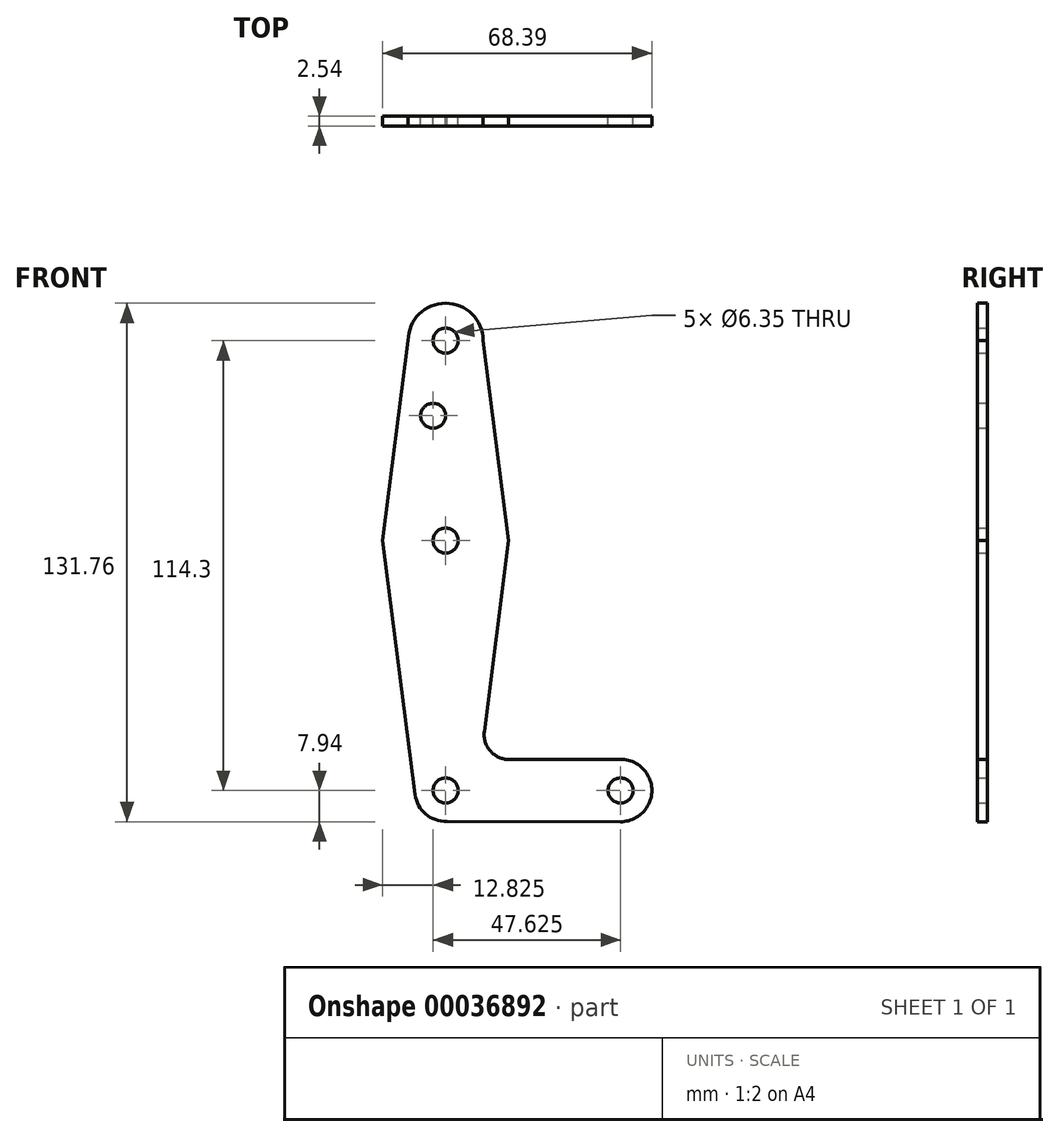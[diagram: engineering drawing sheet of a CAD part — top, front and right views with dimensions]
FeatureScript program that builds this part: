
annotation { "Feature Type Name" : "Feature", "Feature Type Description" : "" }
export const myFeature = defineFeature(function(context is Context, id is Id, definition is map)
    precondition{}
    {
        {
            var Q0;
            Q0=qCreatedBy(makeId("Front.planeOp"),FACE);
            var sketch = newSketch(context, id + "F0", { "sketchPlane" : qUnion([Q0])});
            skLineSegment(sketch, "E0", {"start": v(0, 50.8) * mm, "end": v(0, -63.5) * mm});
            skLineSegment(sketch, "E1", {"start": v(0, -63.5) * mm, "end": v(44.45, -63.5) * mm});
            skCircle(sketch, "E2", {"center": v(0, 50.8) * mm, "radius": 9.53 * mm});
            skCircle(sketch, "E3", {"center": v(0, 0) * mm, "radius": 15.88 * mm});
            skCircle(sketch, "E4", {"center": v(0, -63.5) * mm, "radius": 7.84 * mm});
            skCircle(sketch, "E5", {"center": v(44.45, -63.5) * mm, "radius": 7.94 * mm});
            skLineSegment(sketch, "E6", {"start": v(-9.52, 50.8) * mm, "end": v(-16, 0) * mm});
            skLineSegment(sketch, "E7", {"start": v(9.53, 50.8) * mm, "end": v(16, 0) * mm});
            skLineSegment(sketch, "E8", {"start": v(16, 0) * mm, "end": v(9.82, -48.47) * mm});
            skLineSegment(sketch, "E9", {"start": v(16.13, -55.62) * mm, "end": v(44.43, -55.56) * mm});
            skCircle(sketch, "E10", {"center": v(0, 50.8) * mm, "radius": 3.18 * mm});
            skCircle(sketch, "E11", {"center": v(44.45, -63.5) * mm, "radius": 3.18 * mm});
            skCircle(sketch, "E12", {"center": v(-3.17, 31.72) * mm, "radius": 3.18 * mm});
            skCircle(sketch, "E13", {"center": v(0, 0) * mm, "radius": 3.18 * mm});
            skLineSegment(sketch, "E14", {"start": v(-16, 0) * mm, "end": v(-7.78, -64.5) * mm});
            skCircle(sketch, "E15", {"center": v(0, -63.5) * mm, "radius": 3.18 * mm});
            skArc(sketch, "E16.filletArc", {"start": v(9.82, -48.47) * mm, "mid": v(11.36, -53.48) * mm, "end": v(16.13, -55.62) * mm});
            skLineSegment(sketch, "E17", {"start": v(0.28, -71.34) * mm, "end": v(44.43, -71.44) * mm});
            skSolve(sketch);
        }
        {
            var Q0;
            Q0 = qSketchRegion(id + "F0", true);
            extrude(context, id + "F1", {"entities" : qUnion([Q0]), "depth" : 2.54 * mm});
        }
        {
            var Q0;
            {var subQ0=sQuery(id+"F0.wireOp",EDGE,"E4");var subQ3=sQuery(id+"F0.wireOp",EDGE,"E0");var subQ4=makeQuery(id+"F0.imprint","INTERSECT",VERTEX,{"derivedFrom":[subQ3,subQ0]});Q0=makeQuery(id+"F0.imprint","IMPRINT",FACE,{"disambiguationData":[TD([[makeQuery(id+"F0.imprint","IMPRINT",EDGE,{"disambiguationData":[TD([[subQ4,-1.0]])],"derivedFrom":subQ3}),1.0]])]});}
            extrude(context, id + "F2", {"entities" : qUnion([Q0]), "operationType" : NewBodyOperationType.ADD, "depth" : 2.54 * mm});
        }
    });
